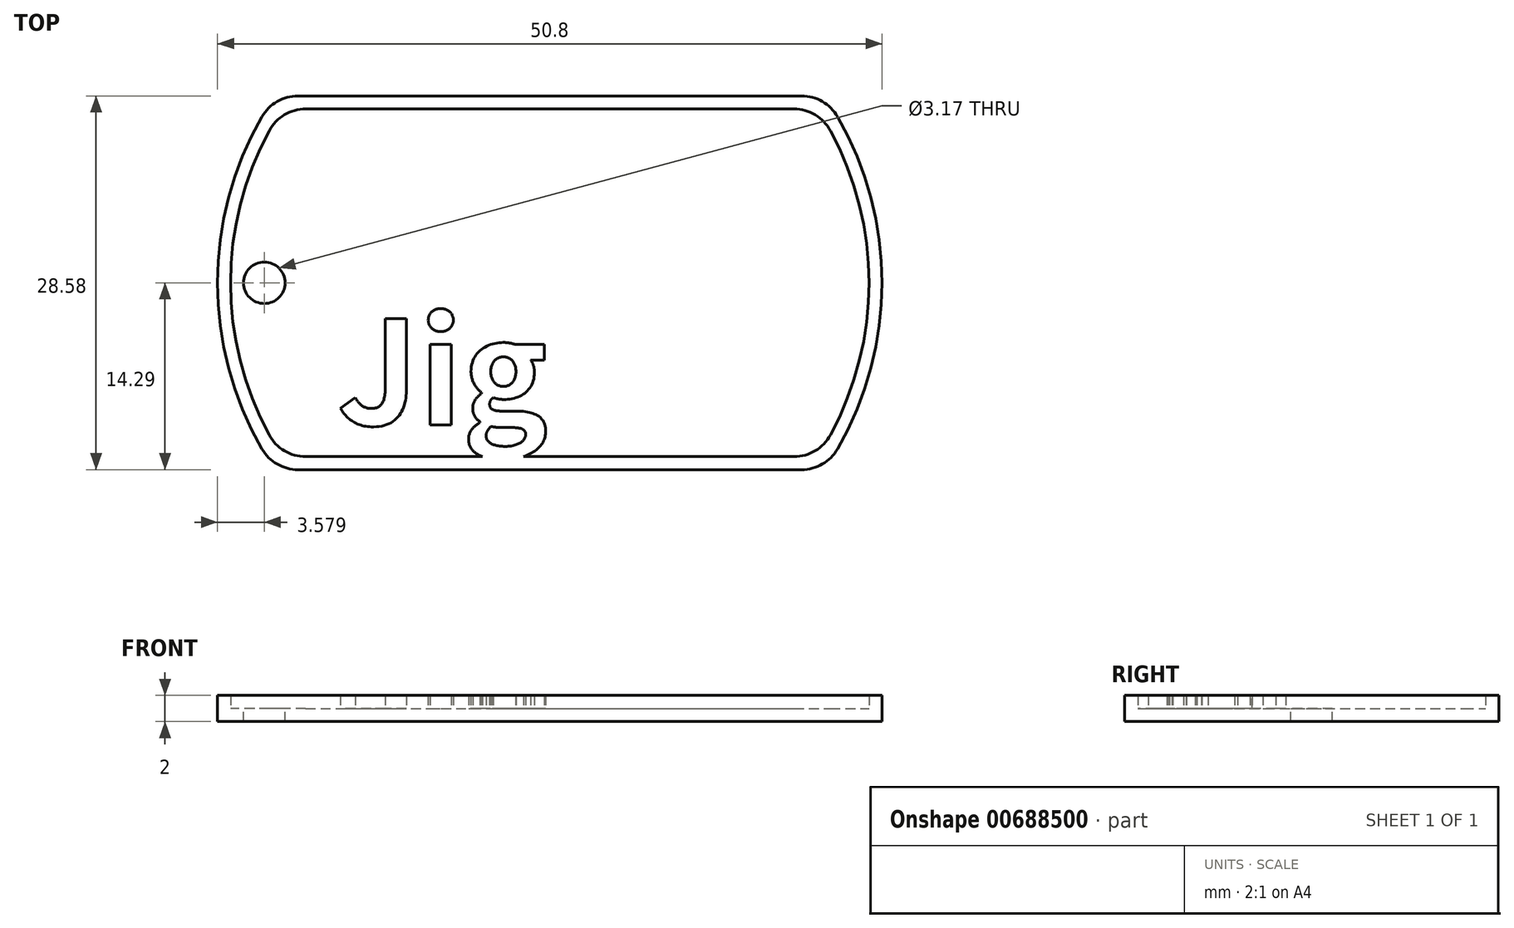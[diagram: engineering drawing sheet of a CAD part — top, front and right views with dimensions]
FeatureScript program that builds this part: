
annotation { "Feature Type Name" : "Feature", "Feature Type Description" : "" }
export const myFeature = defineFeature(function(context is Context, id is Id, definition is map)
    precondition{}
    {
        {
            var Q0;
            Q0=qCreatedBy(makeId("Top.planeOp"),FACE);
            var sketch = newSketch(context, id + "F0", { "sketchPlane" : qUnion([Q0])});
            skArc(sketch, "E0", {"start": v(-22, 12.7) * mm, "mid": v(-25.4, 0) * mm, "end": v(-22, -12.7) * mm});
            skLineSegment(sketch, "E1.top", {"start": v(-19.25, -14.29) * mm, "end": v(19.25, -14.29) * mm});
            skArc(sketch, "E2.trimOffspring", {"start": v(22, -12.7) * mm, "mid": v(25.4, 0) * mm, "end": v(22, 12.7) * mm});
            skLineSegment(sketch, "E3", {"start": v(-19.25, 14.29) * mm, "end": v(19.25, 14.29) * mm});
            skPoint(sketch, "E4.visualSharp", {"position": v(-21, 14.29) * mm});
            skArc(sketch, "E4.filletArc", {"start": v(-19.25, 14.29) * mm, "mid": v(-20.83, 13.86) * mm, "end": v(-22, 12.7) * mm});
            skPoint(sketch, "E5.visualSharp", {"position": v(21, 14.29) * mm});
            skArc(sketch, "E5.filletArc", {"start": v(22, 12.7) * mm, "mid": v(20.83, 13.86) * mm, "end": v(19.25, 14.29) * mm});
            skPoint(sketch, "E6.visualSharp", {"position": v(21, -14.29) * mm});
            skArc(sketch, "E6.filletArc", {"start": v(19.25, -14.29) * mm, "mid": v(20.83, -13.86) * mm, "end": v(22, -12.7) * mm});
            skPoint(sketch, "E7.visualSharp", {"position": v(-21, -14.29) * mm});
            skArc(sketch, "E7.filletArc", {"start": v(-22, -12.7) * mm, "mid": v(-20.83, -13.86) * mm, "end": v(-19.25, -14.29) * mm});
            skSolve(sketch);
        }
        {
            var Q0;
            Q0=makeQuery(id+"F0.imprint","IMPRINT",FACE,{"disambiguationData":[TD([[makeQuery(id+"F0.imprint","IMPRINT",EDGE,{"derivedFrom":sQuery(id+"F0.wireOp",EDGE,"E0")}),1.0]])]});
            extrude(context, id + "F1", {"entities" : qUnion([Q0]), "depth" : 1 * mm, "offsetDistance" : 25.4 * mm});
        }
        {
            var Q0;
            Q0=makeQuery(id+"F1.opExtrude","CAP_FACE",FACE,{"disambiguationData":[OSD([sQuery(id+"F0.wireOp",EDGE,"E0"),sQuery(id+"F0.wireOp",EDGE,"E1.top"),sQuery(id+"F0.wireOp",EDGE,"E2.trimOffspring"),sQuery(id+"F0.wireOp",EDGE,"E3"),sQuery(id+"F0.wireOp",EDGE,"E4.filletArc"),sQuery(id+"F0.wireOp",EDGE,"E5.filletArc"),sQuery(id+"F0.wireOp",EDGE,"E6.filletArc"),sQuery(id+"F0.wireOp",EDGE,"E7.filletArc")])],"isStart":false});
            var sketch = newSketch(context, id + "F2", { "sketchPlane" : qUnion([Q0])});
            skLineSegment(sketch, "E8.0", {"start": v(-18.66, 13.29) * mm, "end": v(18.66, 13.29) * mm});
            skArc(sketch, "E8.1", {"start": v(-21.45, 11.63) * mm, "mid": v(-24.4, 0) * mm, "end": v(-21.45, -11.63) * mm});
            skLineSegment(sketch, "E8.2", {"start": v(-18.66, -13.29) * mm, "end": v(18.66, -13.29) * mm});
            skArc(sketch, "E8.3", {"start": v(21.45, -11.63) * mm, "mid": v(24.4, 0) * mm, "end": v(21.45, 11.63) * mm});
            skPoint(sketch, "E9.visualSharp", {"position": v(-20.46, 13.29) * mm});
            skArc(sketch, "E9.filletArc", {"start": v(-18.66, 13.29) * mm, "mid": v(-20.29, 12.84) * mm, "end": v(-21.45, 11.63) * mm});
            skPoint(sketch, "E10.visualSharp", {"position": v(20.46, 13.29) * mm});
            skArc(sketch, "E10.filletArc", {"start": v(21.45, 11.63) * mm, "mid": v(20.29, 12.84) * mm, "end": v(18.66, 13.29) * mm});
            skPoint(sketch, "E11.visualSharp", {"position": v(20.46, -13.29) * mm});
            skArc(sketch, "E11.filletArc", {"start": v(18.66, -13.29) * mm, "mid": v(20.29, -12.84) * mm, "end": v(21.45, -11.63) * mm});
            skPoint(sketch, "E12.visualSharp", {"position": v(-20.46, -13.29) * mm});
            skArc(sketch, "E12.filletArc", {"start": v(-21.45, -11.63) * mm, "mid": v(-20.29, -12.84) * mm, "end": v(-18.66, -13.29) * mm});
            skLineSegment(sketch, "E13.0", {"start": v(-19.25, 14.29) * mm, "end": v(19.25, 14.29) * mm});
            skArc(sketch, "E13.1", {"start": v(-22, 12.7) * mm, "mid": v(-25.4, 0) * mm, "end": v(-22, -12.7) * mm});
            skLineSegment(sketch, "E13.2", {"start": v(-19.25, -14.29) * mm, "end": v(19.25, -14.29) * mm});
            skArc(sketch, "E13.3", {"start": v(22, -12.7) * mm, "mid": v(25.4, 0) * mm, "end": v(22, 12.7) * mm});
            skPoint(sketch, "E14.visualSharp", {"position": v(-21, -14.29) * mm});
            skArc(sketch, "E14.filletArc", {"start": v(-22, -12.7) * mm, "mid": v(-20.83, -13.86) * mm, "end": v(-19.25, -14.29) * mm});
            skPoint(sketch, "E15.visualSharp", {"position": v(21, -14.29) * mm});
            skArc(sketch, "E15.filletArc", {"start": v(19.25, -14.29) * mm, "mid": v(20.83, -13.86) * mm, "end": v(22, -12.7) * mm});
            skPoint(sketch, "E16.visualSharp", {"position": v(21, 14.29) * mm});
            skArc(sketch, "E16.filletArc", {"start": v(22, 12.7) * mm, "mid": v(20.83, 13.86) * mm, "end": v(19.25, 14.29) * mm});
            skPoint(sketch, "E17.visualSharp", {"position": v(-21, 14.29) * mm});
            skArc(sketch, "E17.filletArc", {"start": v(-19.25, 14.29) * mm, "mid": v(-20.83, 13.86) * mm, "end": v(-22, 12.7) * mm});
            skSolve(sketch);
        }
        {
            var Q0;
            Q0=makeQuery(id+"F2.imprint","IMPRINT",FACE,{"disambiguationData":[TD([[makeQuery(id+"F2.imprint","IMPRINT",EDGE,{"derivedFrom":sQuery(id+"F2.wireOp",EDGE,"E8.0")}),1.0]])]});
            extrude(context, id + "F3", {"entities" : qUnion([Q0]), "operationType" : NewBodyOperationType.ADD, "depth" : 1 * mm, "offsetDistance" : 25.4 * mm});
        }
        {
            var Q0;
            Q0=makeQuery(id+"F1.opExtrude","CAP_FACE",FACE,{"disambiguationData":[OSD([sQuery(id+"F0.wireOp",EDGE,"E0"),sQuery(id+"F0.wireOp",EDGE,"E1.top"),sQuery(id+"F0.wireOp",EDGE,"E2.trimOffspring"),sQuery(id+"F0.wireOp",EDGE,"E3"),sQuery(id+"F0.wireOp",EDGE,"E4.filletArc"),sQuery(id+"F0.wireOp",EDGE,"E5.filletArc"),sQuery(id+"F0.wireOp",EDGE,"E6.filletArc"),sQuery(id+"F0.wireOp",EDGE,"E7.filletArc")])],"isStart":false});
            var sketch = newSketch(context, id + "F4", { "sketchPlane" : qUnion([Q0])});
            skCircle(sketch, "E18", {"center": v(-21.82, 0) * mm, "radius": 1.59 * mm});
            skSolve(sketch);
        }
        {
            var Q0;
            Q0=makeQuery(id+"F4.imprint","IMPRINT",FACE,{"disambiguationData":[TD([[makeQuery(id+"F4.imprint","IMPRINT",EDGE,{"derivedFrom":sQuery(id+"F4.wireOp",EDGE,"E18")}),1.0]])]});
            extrude(context, id + "F5", {"entities" : qUnion([Q0]), "operationType" : NewBodyOperationType.REMOVE, "oppositeDirection" : true, "depth" : 1 * mm, "offsetDistance" : 25.4 * mm});
        }
        {
            var Q0;
            Q0=qCreatedBy(makeId("Top.planeOp"),FACE);
            var sketch = newSketch(context, id + "F6", { "sketchPlane" : qUnion([Q0])});
            skText(sketch, "E19", { "text": "Ron", "fontName": "NotoSansCJKkr-Bold.otf"});
            const initialGuessF6  = {"E19": [-0.01032, 0, 1, 0, 0.00946]};
            skSetInitialGuess(sketch, initialGuessF6);
            skSolve(sketch);
        }
        {
            var Q0;
            Q0=makeQuery(id+"F2.imprint","IMPRINT",FACE,{"disambiguationData":[TD([[makeQuery(id+"F2.imprint","IMPRINT",EDGE,{"derivedFrom":sQuery(id+"F2.wireOp",EDGE,"E8.0")}),-1.0]])]});
            var sketch = newSketch(context, id + "F7", { "sketchPlane" : qUnion([Q0])});
            skText(sketch, "E20", { "text": "Jig", "fontName": "NotoSansCJKjp-Bold.otf"});
            const initialGuessF7  = {"E20": [-0.01624, -0.01086, 1, 0, 0.0079]};
            skSetInitialGuess(sketch, initialGuessF7);
            skSolve(sketch);
        }
        {
            var Q0;
            Q0 = qSketchRegion(id + "F7", true);
            extrude(context, id + "F8", {"entities" : qUnion([Q0]), "operationType" : NewBodyOperationType.ADD, "depth" : 1 * mm, "offsetDistance" : 25.4 * mm});
        }
        {
            var Q0;
            Q0 = qSketchRegion(id + "F6", true);
            extrude(context, id + "F9", {"entities" : qUnion([Q0]), "operationType" : NewBodyOperationType.ADD, "depth" : 1 * mm, "offsetDistance" : 25.4 * mm});
        }
    });
